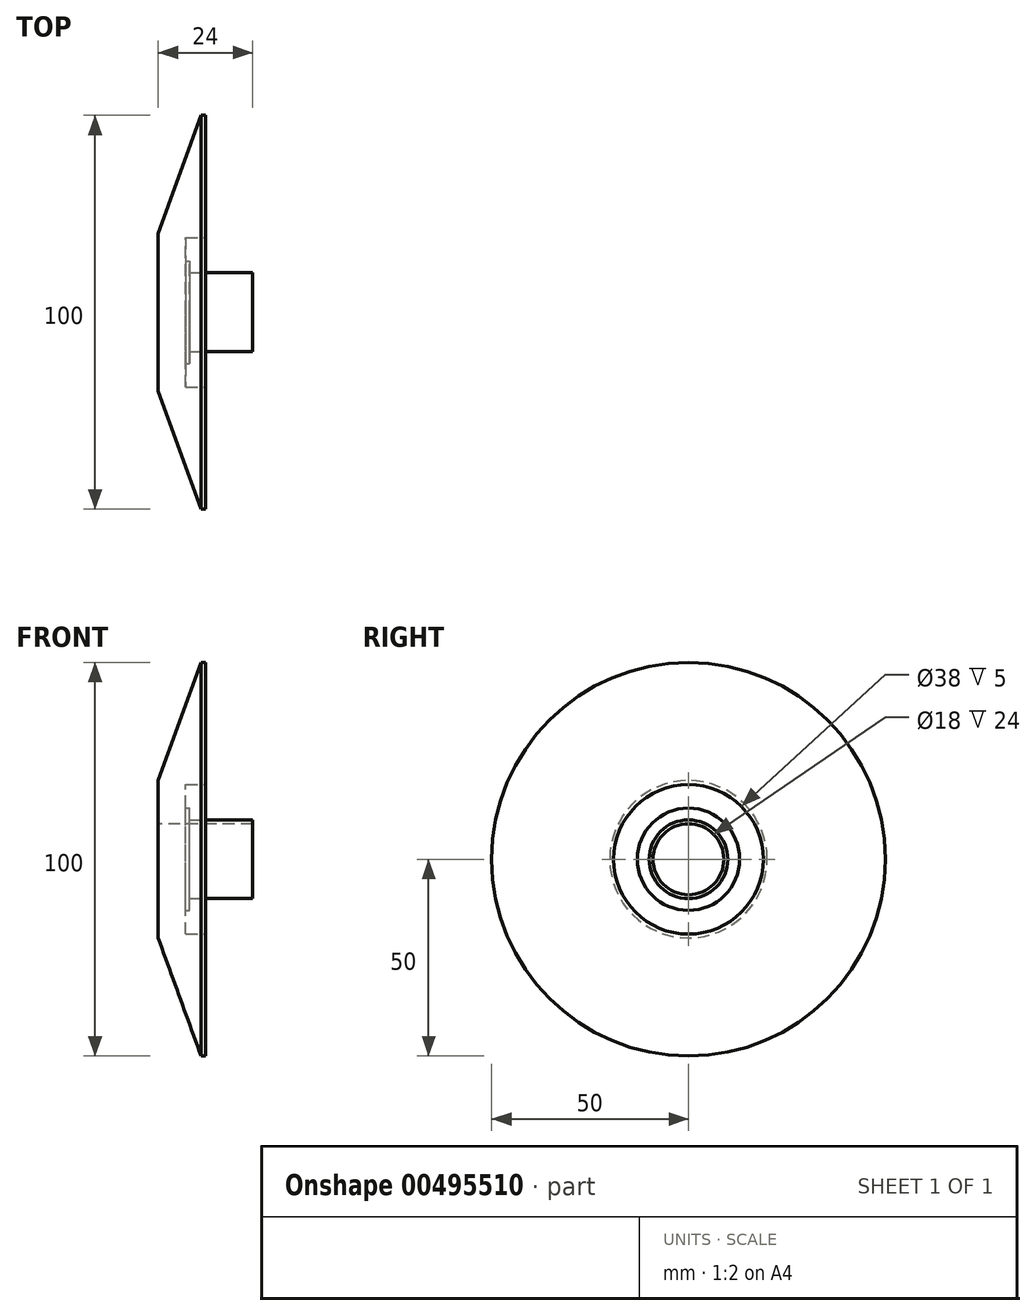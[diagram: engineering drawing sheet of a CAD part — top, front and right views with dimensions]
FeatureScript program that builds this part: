
annotation { "Feature Type Name" : "Feature", "Feature Type Description" : "" }
export const myFeature = defineFeature(function(context is Context, id is Id, definition is map)
    precondition{}
    {
        {
            var Q0;
            Q0=qCreatedBy(makeId("Front.planeOp"),FACE);
            var sketch = newSketch(context, id + "F0", { "sketchPlane" : qUnion([Q0])});
            skLineSegment(sketch, "E0", {"start": v(0, 20) * mm, "end": v(10.92, 50) * mm});
            skLineSegment(sketch, "E1", {"start": v(10.92, 50) * mm, "end": v(12, 50) * mm});
            skLineSegment(sketch, "E2", {"start": v(12, 50) * mm, "end": v(12, 19) * mm});
            skLineSegment(sketch, "E3", {"start": v(12, 10) * mm, "end": v(24, 10) * mm});
            skLineSegment(sketch, "E4", {"start": v(24, 10) * mm, "end": v(24, 0) * mm});
            skLineSegment(sketch, "E5", {"start": v(24, 0) * mm, "end": v(0, 0) * mm});
            skLineSegment(sketch, "E6", {"start": v(0, 0) * mm, "end": v(0, 20) * mm});
            skLineSegment(sketch, "E7.bottom", {"start": v(8, 10) * mm, "end": v(12, 10) * mm});
            skLineSegment(sketch, "E7.top", {"start": v(7, 19) * mm, "end": v(12, 19) * mm});
            skLineSegment(sketch, "E7.left", {"start": v(7, 13) * mm, "end": v(7, 19) * mm});
            skLineSegment(sketch, "E8.bottom", {"start": v(7, 13) * mm, "end": v(8, 13) * mm});
            skLineSegment(sketch, "E8.right", {"start": v(8, 13) * mm, "end": v(8, 10) * mm});
            skPoint(sketch, "E7.right.end.orphan", {"position": v(12, 13) * mm});
            skSolve(sketch);
        }
        {
            var Q0;
            Q0=makeQuery(id+"F0.imprint","IMPRINT",FACE,{"disambiguationData":[TD([[makeQuery(id+"F0.imprint","IMPRINT",EDGE,{"derivedFrom":sQuery(id+"F0.wireOp",EDGE,"E0")}),-1.0]])]});
            var Q1;
            Q1=sQuery(id+"F0.wireOp",EDGE,"E5");
            revolve(context, id + "F1", {"entities" : qUnion([Q0]), "axis" : qUnion([Q1]), "revolveType" : RevolveType.FULL});
        }
        {
            var Q0;
            Q0=qCreatedBy(makeId("Right.planeOp"),FACE);
            var sketch = newSketch(context, id + "F2", { "sketchPlane" : qUnion([Q0])});
            skPoint(sketch, "E9", {"position": v(0, 0) * mm});
            skSolve(sketch);
        }
        {
            var Q0;
            Q0=sQuery(id+"F2.wireOp",VERTEX,"E9");
            var Q1;
            Q1=makeQuery(id+"F1.opRevolve","SWEPT_BODY",BODY,{"disambiguationData":[OSD([sQuery(id+"F0.wireOp",EDGE,"E0"),sQuery(id+"F0.wireOp",EDGE,"E1"),sQuery(id+"F0.wireOp",EDGE,"E2"),sQuery(id+"F0.wireOp",EDGE,"E3"),sQuery(id+"F0.wireOp",EDGE,"E4"),sQuery(id+"F0.wireOp",EDGE,"E5"),sQuery(id+"F0.wireOp",EDGE,"E6")])]});
            hole(context, id + "F3", {"style" : HoleStyle.SIMPLE, "endStyle" : HoleEndStyle.THROUGH, "oppositeDirection" : true, "holeDiameter" : 18 * mm, "isTappedThrough" : true, "tappedDepth" : 12 * mm, "tapClearance" : 3, "locations" : qUnion([Q0]), "scope" : qUnion([Q1])});
        }
    });
